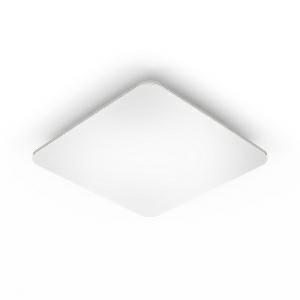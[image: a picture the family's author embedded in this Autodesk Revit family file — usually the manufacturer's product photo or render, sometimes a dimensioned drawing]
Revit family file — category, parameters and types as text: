
# Revit family: rs_pro_led_q1_007126
name_source: partatom
category: Leuchten
revit_build: Autodesk Revit 2016 (Build: 20190508_0715(x64)
units: mm (PartAtom-declared; Revit-internal decimal feet)

## family parameters
Basisbauteil = Fläche
Beim Laden mit Abzugskörper schneiden = Nein
Bemaßung runder Anschluss = Durchmesser verwenden
Gemeinsam genutzt = Nein
Lichtquelle = Nein
Raumberechnungspunkt = Nein
Teiletyp = Normal

## types (1)
- RS PRO LED Q1 (1 x , 2350 lm, 3000 K)
    Beschreibung = Dimensions (L x W x H): 56 x 331 x 331 mm; Mains power supply: 220 – 240 V / 50 – 60 Hz; Sensor Technology: High frequency; Transmitter power: < 1 mW; HF-system: 5,8 GHz; Output: 26 W; Interconnection: Yes; Type of interconnection: Master/master, Master/slave; Luminous flux: 2350 lm; Colour temperature: 3000 K; Colour variation LED: SDCM3; Colour Rendering Index CRI: 80-89; With lamp: Yes, STEINEL LED system; Lamp: LED cannot be replaced; LED life expectancy (max. °C): 50000 h; Drop in luminous flux in accordance with LM80: L70B10; Base: without; LED cooling system: Passive Thermo Control; With motion detector: Yes; Detection: also through glass, wood and stud walls; Detection angle: 360 °; Angle of aperture: 160 °; Capability of masking out individual segments: Yes; Electronic scalability: Yes; Mechanical scalability: No; Reach, radial: Ø 8 m (50 m²); Reach, tangential: Ø 8 m (50 m²); Main light adjustable: 50 - 100 %; Continuous light: selectable; Photo-cell controller: Yes; Twilight setting: 2 – 2000 lx; Time setting: 5 sec – 15 min; Basic light level function: Yes; Basic light level function time: 10/30 min, all night; Functions: Group parameterisation, Manual ON / ON-OFF, Master/slave override, Neighbouring-group function; Soft light start: Yes; Impact resistance: IK03; IP-rating: IP20; Protection class: II; Ambient temperature: -10 – 50 °C; Housing material: Aluminium; Cover material: Plastic, opal; Manufacturer's Warranty: 5 years; Settings via: DIP switches, Potentiometers, Remote control, Smart Remote; With remote control: No; Version: warm white silver; PU1, EAN: 4007841007126
    CIE Flux Codes = 46 77 95 100 100
    Color Rendering = 80-89
    Color Temperature = 3000 K
    Frequency = 60 Hz, 50 Hz
    Height = 331 mm
    Hersteller = Steinel
    Lamp Light Flux = 2350 lm
    Lamp count = 1
    Lampe = 1 x
    Length = 56 mm
    Luminous efficacy = 90 lm/W
    ModVariant = Nein
    Modell = 007126
    Mounting Type = Surface mounted
    Number of Poles = 1
    OnlyDefault = Ja
    Power Factor = 1
    Product Name = RS PRO LED Q1
    Product group = Sensor-switched indoor light
    ProductGroupID = 30
    Protection Class = Protection class II
    Protection Degree = IP 20
    RlxData = <blob elided: 27837 chars, md5=cf7aae2f>
    Scheinlast = 26 VA
    Socket = socket
    Standby Power = 0 W
    System Light Flux = 2350 lm
    System Power = 26 W
    Typenbild = produkt1_007126.jpg
    Typenkommentare = Product without accessories
    URL = http://relux.com
    VarID = ---
    Voltage = 0 V
    Vorgabe-Ansicht = 1800 mm
    Weight = 0.00 kg
    Width = 331 mm

## geometry (parser evidence)
native form markers: Blend x4, Sweep x8
no freeform markers — native parametric forms only
